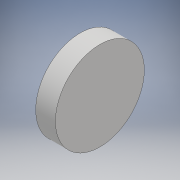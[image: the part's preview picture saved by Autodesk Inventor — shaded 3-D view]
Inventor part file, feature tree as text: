
AUTODESK INVENTOR PART (.ipt)
format: ipt  version: 2018 (Build 220112000, 112)  size: 91,136 bytes
history: native  units: mm
features: extrude x1, sketch x1
ambient origin geometry x8: Origin, YZ Plane, XZ Plane, XY Plane, X Axis, Y Axis, Z Axis, Center Point
bodies: Solid1 (feature_tree)
feature tree (2):
  extrude  "Extrusion1"  Depth=10.0mm TaperAngle=0.0deg
  sketch  "Sketch1"  dims[d0=45.0mm d1=10.0mm d2=0.0mm]
